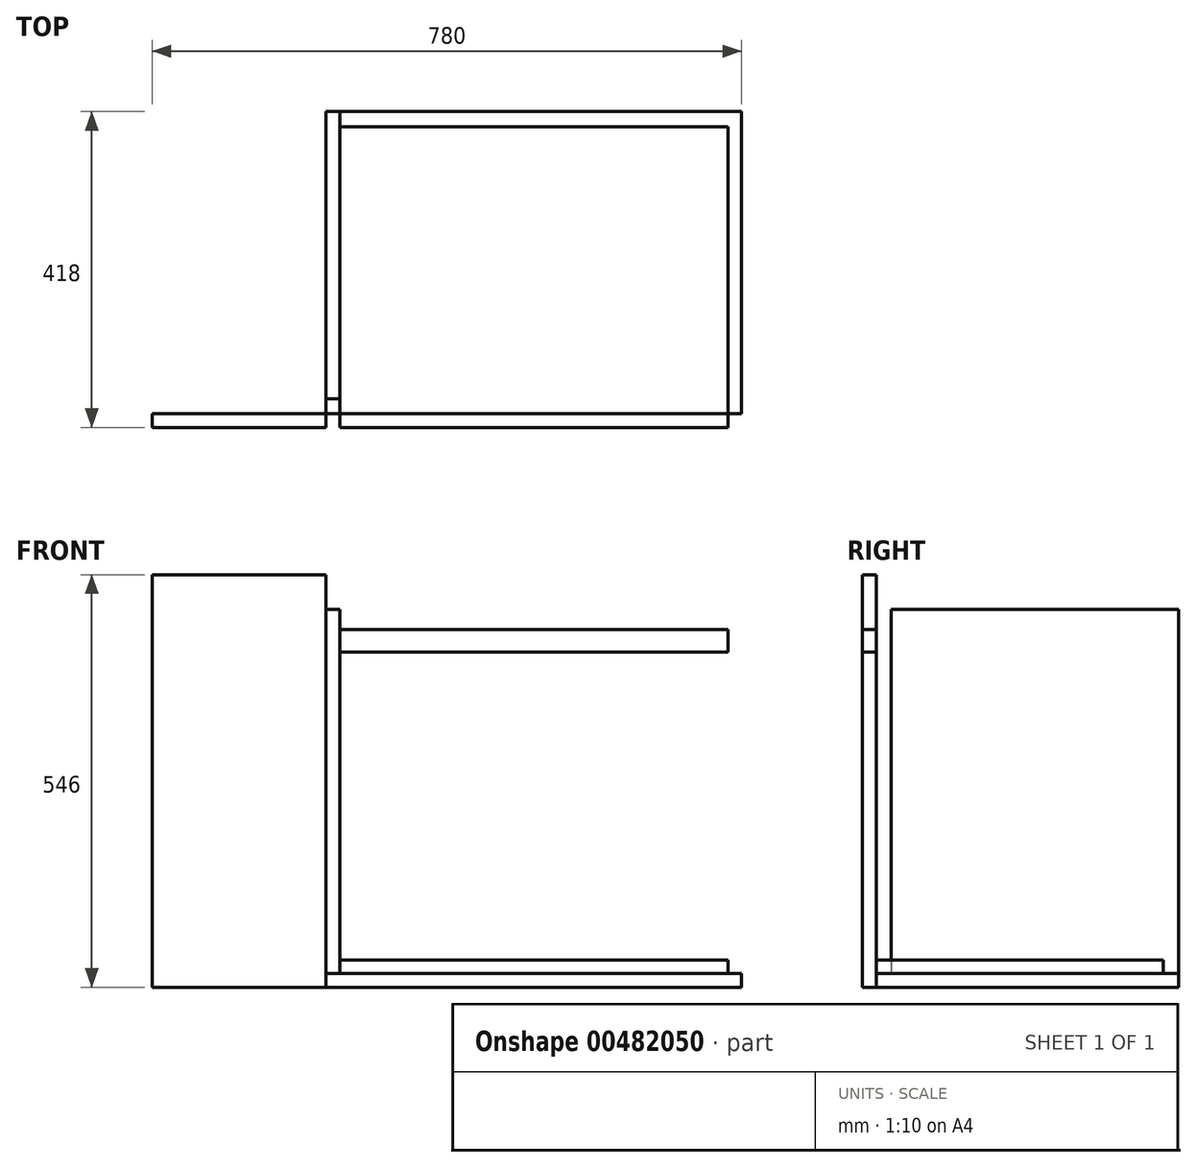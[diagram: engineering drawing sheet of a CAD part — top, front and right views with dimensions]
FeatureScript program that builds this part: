
annotation { "Feature Type Name" : "Feature", "Feature Type Description" : "" }
export const myFeature = defineFeature(function(context is Context, id is Id, definition is map)
    precondition{}
    {
        {
            var Q0;
            Q0=qCreatedBy(makeId("Top.planeOp"),FACE);
            var sketch = newSketch(context, id + "F0", { "sketchPlane" : qUnion([Q0])});
            skLineSegment(sketch, "E0.bottom", {"start": v(0, 0) * mm, "end": v(550, 0) * mm});
            skLineSegment(sketch, "E0.top", {"start": v(0, 400) * mm, "end": v(550, 400) * mm});
            skLineSegment(sketch, "E0.left", {"start": v(0, 0) * mm, "end": v(0, 400) * mm});
            skLineSegment(sketch, "E0.right", {"start": v(550, 0) * mm, "end": v(550, 400) * mm});
            skSolve(sketch);
        }
        {
            var Q0;
            Q0=qSketchRegion(id+"F0",true);
            extrude(context, id + "F1", {"entities" : qUnion([Q0]), "depth" : 18 * mm});
        }
        {
            var Q0;
            Q0=makeQuery(id+"F1.opExtrude","CAP_FACE",FACE,{"disambiguationData":[OSD([sQuery(id+"F0.wireOp",EDGE,"E0.bottom"),sQuery(id+"F0.wireOp",EDGE,"E0.top"),sQuery(id+"F0.wireOp",EDGE,"E0.left"),sQuery(id+"F0.wireOp",EDGE,"E0.right")])],"isStart":false});
            var sketch = newSketch(context, id + "F2", { "sketchPlane" : qUnion([Q0])});
            skLineSegment(sketch, "E1.bottom", {"start": v(0, 400) * mm, "end": v(18, 400) * mm});
            skLineSegment(sketch, "E1.top", {"start": v(0, 20) * mm, "end": v(18, 20) * mm});
            skLineSegment(sketch, "E1.left", {"start": v(0, 400) * mm, "end": v(0, 20) * mm});
            skLineSegment(sketch, "E1.right", {"start": v(18, 400) * mm, "end": v(18, 20) * mm});
            skSolve(sketch);
        }
        {
            var Q0;
            Q0=qSketchRegion(id+"F2",true);
            extrude(context, id + "F3", {"entities" : qUnion([Q0]), "depth" : 482 * mm});
        }
        {
            var Q0;
            Q0=qCreatedBy(makeId("Front.planeOp"),FACE);
            var sketch = newSketch(context, id + "F4", { "sketchPlane" : qUnion([Q0])});
            skLineSegment(sketch, "E2.bottom", {"start": v(532, 473.4) * mm, "end": v(18, 473.4) * mm});
            skLineSegment(sketch, "E2.top", {"start": v(532, 443.4) * mm, "end": v(18, 443.4) * mm});
            skLineSegment(sketch, "E2.left", {"start": v(532, 473.4) * mm, "end": v(532, 443.4) * mm});
            skLineSegment(sketch, "E2.right", {"start": v(18, 473.4) * mm, "end": v(18, 443.4) * mm});
            skSolve(sketch);
        }
        {
            var Q0;
            Q0=qSketchRegion(id+"F4",true);
            extrude(context, id + "F5", {"entities" : qUnion([Q0]), "depth" : 18 * mm});
        }
        {
            var Q0;
            Q0=makeQuery(id+"F1.opExtrude","CAP_FACE",FACE,{"disambiguationData":[OSD([sQuery(id+"F0.wireOp",EDGE,"E0.bottom"),sQuery(id+"F0.wireOp",EDGE,"E0.top"),sQuery(id+"F0.wireOp",EDGE,"E0.left"),sQuery(id+"F0.wireOp",EDGE,"E0.right")])],"isStart":false});
            var sketch = newSketch(context, id + "F6", { "sketchPlane" : qUnion([Q0])});
            skLineSegment(sketch, "E3.bottom", {"start": v(18, 0) * mm, "end": v(532, 0) * mm});
            skLineSegment(sketch, "E3.top", {"start": v(18, 380) * mm, "end": v(532, 380) * mm});
            skLineSegment(sketch, "E3.left", {"start": v(18, 0) * mm, "end": v(18, 380) * mm});
            skLineSegment(sketch, "E3.right", {"start": v(532, 0) * mm, "end": v(532, 380) * mm});
            skSolve(sketch);
        }
        {
            var Q0;
            Q0=qSketchRegion(id+"F6",true);
            extrude(context, id + "F7", {"entities" : qUnion([Q0]), "depth" : 18 * mm});
        }
        {
            var Q0;
            Q0=qCreatedBy(makeId("Front.planeOp"),FACE);
            var sketch = newSketch(context, id + "F8", { "sketchPlane" : qUnion([Q0])});
            skLineSegment(sketch, "E4.bottom", {"start": v(0, 0) * mm, "end": v(-230, 0) * mm});
            skLineSegment(sketch, "E4.top", {"start": v(0, 546) * mm, "end": v(-230, 546) * mm});
            skLineSegment(sketch, "E4.left", {"start": v(0, 0) * mm, "end": v(0, 546) * mm});
            skLineSegment(sketch, "E4.right", {"start": v(-230, 0) * mm, "end": v(-230, 546) * mm});
            skSolve(sketch);
        }
        {
            var Q0;
            Q0=qSketchRegion(id+"F8",true);
            extrude(context, id + "F9", {"entities" : qUnion([Q0]), "depth" : 18 * mm});
        }
    });
